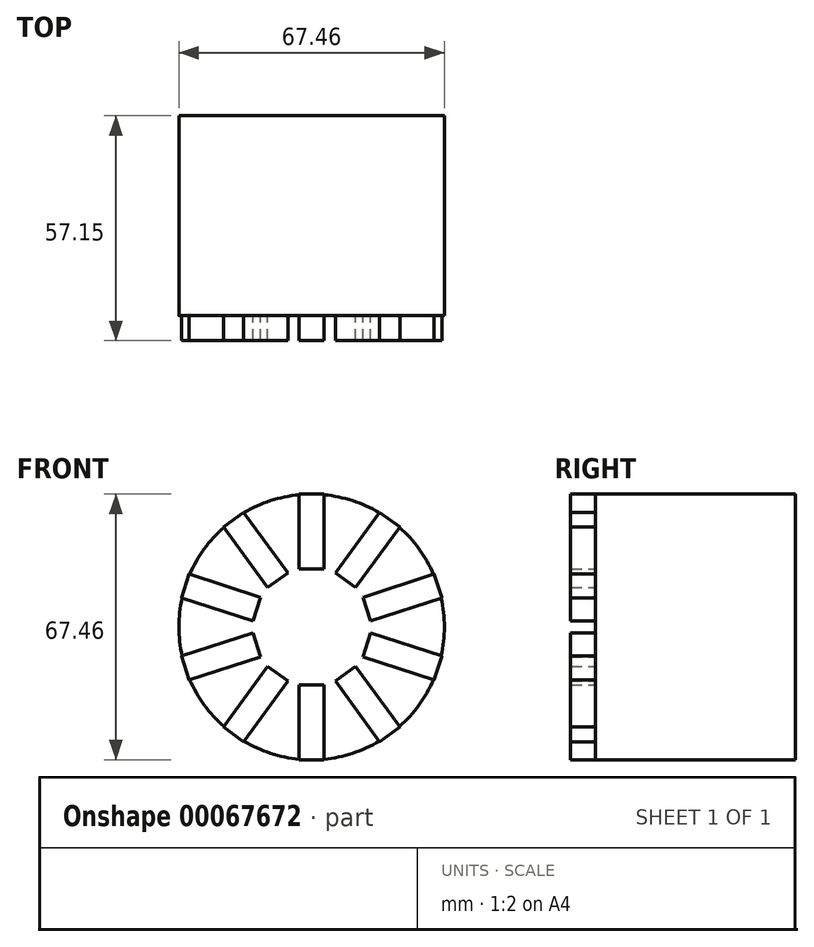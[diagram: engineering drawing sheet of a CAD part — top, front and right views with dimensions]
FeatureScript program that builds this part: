
annotation { "Feature Type Name" : "Feature", "Feature Type Description" : "" }
export const myFeature = defineFeature(function(context is Context, id is Id, definition is map)
    precondition{}
    {
        {
            var Q0;
            Q0=qCreatedBy(makeId("Front.planeOp"),FACE);
            var sketch = newSketch(context, id + "F0", { "sketchPlane" : qUnion([Q0])});
            skCircle(sketch, "E0", {"center": v(0, 0) * mm, "radius": 33.73 * mm});
            skSolve(sketch);
        }
        {
            var Q0;
            Q0=qSketchRegion(id+"F0",true);
            extrude(context, id + "F1", {"entities" : qUnion([Q0]), "endBound" : BoundingType.SYMMETRIC, "depth" : 50.8 * mm});
        }
        {
            var Q0;
            Q0=makeQuery(id+"F1.opExtrude","CAP_FACE",FACE,{"disambiguationData":[OSD([sQuery(id+"F0.wireOp",EDGE,"E0")])],"isStart":false});
            var sketch = newSketch(context, id + "F2", { "sketchPlane" : qUnion([Q0])});
            skLineSegment(sketch, "E1.rect.bottom", {"start": v(-3.18, 14.68) * mm, "end": v(3.17, 14.68) * mm});
            skLineSegment(sketch, "E1.rect.top", {"start": v(-3.18, 33.73) * mm, "end": v(3.17, 33.73) * mm});
            skLineSegment(sketch, "E1.rect.left", {"start": v(-3.18, 14.68) * mm, "end": v(-3.18, 33.73) * mm});
            skLineSegment(sketch, "E1.rect.right", {"start": v(3.17, 14.68) * mm, "end": v(3.17, 33.73) * mm});
            skPoint(sketch, "E1.rect.middle", {"position": v(0, 24.2) * mm});
            skLineSegment(sketch, "E2.1.0", {"start": v(-6.06, 13.74) * mm, "end": v(-17.26, 29.16) * mm});
            skLineSegment(sketch, "E2.1.1", {"start": v(-11.2, 10.01) * mm, "end": v(-6.06, 13.74) * mm});
            skLineSegment(sketch, "E2.1.2", {"start": v(-11.2, 10.01) * mm, "end": v(-22.4, 25.42) * mm});
            skLineSegment(sketch, "E2.1.3", {"start": v(-22.4, 25.42) * mm, "end": v(-17.26, 29.16) * mm});
            skLineSegment(sketch, "E2.2.0", {"start": v(-12.98, 7.56) * mm, "end": v(-31.1, 13.44) * mm});
            skLineSegment(sketch, "E2.2.1", {"start": v(-14.94, 1.52) * mm, "end": v(-12.98, 7.56) * mm});
            skLineSegment(sketch, "E2.2.2", {"start": v(-14.94, 1.52) * mm, "end": v(-33.06, 7.4) * mm});
            skLineSegment(sketch, "E2.2.3", {"start": v(-33.06, 7.4) * mm, "end": v(-31.1, 13.44) * mm});
            skLineSegment(sketch, "E2.3.0", {"start": v(-14.94, -1.52) * mm, "end": v(-33.06, -7.4) * mm});
            skLineSegment(sketch, "E2.3.1", {"start": v(-12.98, -7.56) * mm, "end": v(-14.94, -1.52) * mm});
            skLineSegment(sketch, "E2.3.2", {"start": v(-12.98, -7.56) * mm, "end": v(-31.1, -13.44) * mm});
            skLineSegment(sketch, "E2.3.3", {"start": v(-31.1, -13.44) * mm, "end": v(-33.06, -7.4) * mm});
            skLineSegment(sketch, "E2.4.0", {"start": v(-11.2, -10.01) * mm, "end": v(-22.4, -25.42) * mm});
            skLineSegment(sketch, "E2.4.1", {"start": v(-6.06, -13.74) * mm, "end": v(-11.2, -10.01) * mm});
            skLineSegment(sketch, "E2.4.2", {"start": v(-6.06, -13.74) * mm, "end": v(-17.26, -29.16) * mm});
            skLineSegment(sketch, "E2.4.3", {"start": v(-17.26, -29.16) * mm, "end": v(-22.4, -25.42) * mm});
            skLineSegment(sketch, "E2.5.0", {"start": v(-3.17, -14.68) * mm, "end": v(-3.18, -33.73) * mm});
            skLineSegment(sketch, "E2.5.1", {"start": v(3.18, -14.68) * mm, "end": v(-3.17, -14.68) * mm});
            skLineSegment(sketch, "E2.5.2", {"start": v(3.18, -14.68) * mm, "end": v(3.17, -33.73) * mm});
            skLineSegment(sketch, "E2.5.3", {"start": v(3.17, -33.73) * mm, "end": v(-3.18, -33.73) * mm});
            skLineSegment(sketch, "E2.6.0", {"start": v(6.06, -13.74) * mm, "end": v(17.26, -29.16) * mm});
            skLineSegment(sketch, "E2.6.1", {"start": v(11.2, -10.01) * mm, "end": v(6.06, -13.74) * mm});
            skLineSegment(sketch, "E2.6.2", {"start": v(11.2, -10.01) * mm, "end": v(22.4, -25.42) * mm});
            skLineSegment(sketch, "E2.6.3", {"start": v(22.4, -25.42) * mm, "end": v(17.26, -29.16) * mm});
            skLineSegment(sketch, "E2.7.0", {"start": v(12.98, -7.56) * mm, "end": v(31.1, -13.44) * mm});
            skLineSegment(sketch, "E2.7.1", {"start": v(14.94, -1.52) * mm, "end": v(12.98, -7.56) * mm});
            skLineSegment(sketch, "E2.7.2", {"start": v(14.94, -1.52) * mm, "end": v(33.06, -7.4) * mm});
            skLineSegment(sketch, "E2.7.3", {"start": v(33.06, -7.4) * mm, "end": v(31.1, -13.44) * mm});
            skLineSegment(sketch, "E2.8.0", {"start": v(14.94, 1.52) * mm, "end": v(33.06, 7.4) * mm});
            skLineSegment(sketch, "E2.8.1", {"start": v(12.98, 7.56) * mm, "end": v(14.94, 1.52) * mm});
            skLineSegment(sketch, "E2.8.2", {"start": v(12.98, 7.56) * mm, "end": v(31.1, 13.44) * mm});
            skLineSegment(sketch, "E2.8.3", {"start": v(31.1, 13.44) * mm, "end": v(33.06, 7.4) * mm});
            skLineSegment(sketch, "E2.9.0", {"start": v(11.2, 10.01) * mm, "end": v(22.4, 25.42) * mm});
            skLineSegment(sketch, "E2.9.1", {"start": v(6.06, 13.74) * mm, "end": v(11.2, 10.01) * mm});
            skLineSegment(sketch, "E2.9.2", {"start": v(6.06, 13.74) * mm, "end": v(17.26, 29.16) * mm});
            skLineSegment(sketch, "E2.9.3", {"start": v(17.26, 29.16) * mm, "end": v(22.4, 25.42) * mm});
            skPoint(sketch, "E2.center", {"position": v(0, 0) * mm});
            skSolve(sketch);
        }
        {
            var Q0;
            Q0=qSketchRegion(id+"F2",true);
            extrude(context, id + "F3", {"entities" : qUnion([Q0]), "operationType" : NewBodyOperationType.ADD, "depth" : 6.35 * mm});
        }
    });
